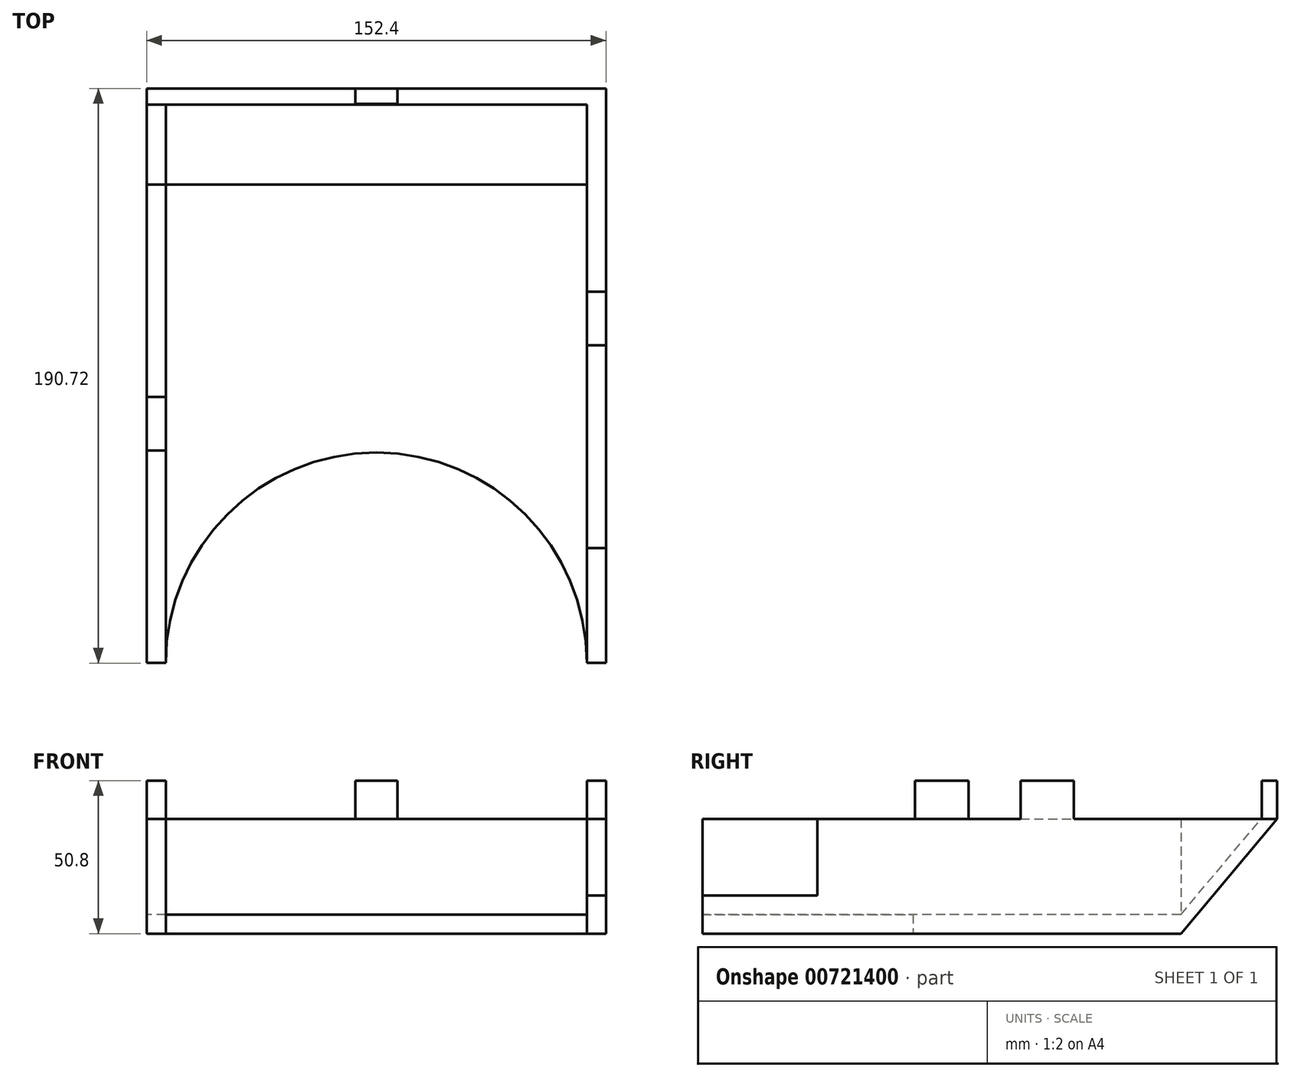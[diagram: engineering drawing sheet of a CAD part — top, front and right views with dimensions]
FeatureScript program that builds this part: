
annotation { "Feature Type Name" : "Feature", "Feature Type Description" : "" }
export const myFeature = defineFeature(function(context is Context, id is Id, definition is map)
    precondition{}
    {
        {
            var Q0;
            Q0=qCreatedBy(makeId("Top.planeOp"),FACE);
            var sketch = newSketch(context, id + "F0", { "sketchPlane" : qUnion([Q0])});
            skLineSegment(sketch, "E0.bottom", {"start": v(76.2, 79.38) * mm, "end": v(-76.2, 79.37) * mm});
            skLineSegment(sketch, "E0.top", {"start": v(76.2, -79.38) * mm, "end": v(-76.2, -79.38) * mm});
            skLineSegment(sketch, "E0.left", {"start": v(76.2, 79.38) * mm, "end": v(76.2, -79.38) * mm});
            skLineSegment(sketch, "E0.right", {"start": v(-76.2, 79.38) * mm, "end": v(-76.2, -79.38) * mm});
            skPoint(sketch, "E0.middle", {"position": v(0, 0) * mm});
            skLineSegment(sketch, "E1", {"start": v(-69.85, -79.38) * mm, "end": v(-69.85, 79.37) * mm});
            skLineSegment(sketch, "E2", {"start": v(69.85, 79.38) * mm, "end": v(69.85, -79.38) * mm});
            skArc(sketch, "E3", {"start": v(69.85, -79.38) * mm, "mid": v(0, -9.52) * mm, "end": v(-69.85, -79.38) * mm});
            skSolve(sketch);
        }
        {
            var Q0;
            {var subQ0=sQuery(id+"F0.wireOp",EDGE,"E1");Q0=makeQuery(id+"F0.imprint","IMPRINT",FACE,{"disambiguationData":[TD([[makeQuery(id+"F0.imprint","IMPRINT",EDGE,{"derivedFrom":subQ0}),-1.0]])]});}
            extrude(context, id + "F1", {"entities" : qUnion([Q0]), "depth" : 6.35 * mm, "offsetDistance" : 25.4 * mm});
        }
        {
            var Q0;
            {var subQ0=sQuery(id+"F0.wireOp",EDGE,"E0.left");Q0=makeQuery(id+"F0.imprint","IMPRINT",FACE,{"disambiguationData":[TD([[makeQuery(id+"F0.imprint","IMPRINT",EDGE,{"derivedFrom":subQ0}),-1.0]])]});}
            var Q1;
            {var subQ0=sQuery(id+"F0.wireOp",EDGE,"E0.right");Q1=makeQuery(id+"F0.imprint","IMPRINT",FACE,{"disambiguationData":[TD([[makeQuery(id+"F0.imprint","IMPRINT",EDGE,{"derivedFrom":subQ0}),1.0]])]});}
            extrude(context, id + "F2", {"entities" : qUnion([Q0, Q1]), "operationType" : NewBodyOperationType.ADD, "depth" : 38.1 * mm, "offsetDistance" : 25.4 * mm});
        }
        {
            var Q0;
            Q0=makeQuery(id+"F2.opExtrude","SWEPT_FACE",FACE,{"disambiguationData":[OSD([sQuery(id+"F0.wireOp",EDGE,"E0.left")])]});
            var sketch = newSketch(context, id + "F3", { "sketchPlane" : qUnion([Q0])});
            skLineSegment(sketch, "E4", {"start": v(79.38, 0) * mm, "end": v(111.34, 38.1) * mm});
            skLineSegment(sketch, "E5", {"start": v(111.34, 38.1) * mm, "end": v(79.38, 38.1) * mm});
            skLineSegment(sketch, "E6", {"start": v(79.38, 6.35) * mm, "end": v(106.02, 38.1) * mm});
            skSolve(sketch);
        }
        {
            var Q0;
            {var subQ0=sQuery(id+"F3.wireOp",EDGE,"E4");Q0=makeQuery(id+"F3.imprint","IMPRINT",FACE,{"disambiguationData":[TD([[makeQuery(id+"F3.imprint","IMPRINT",EDGE,{"derivedFrom":subQ0}),1.0]])]});}
            extrude(context, id + "F4", {"entities" : qUnion([Q0]), "operationType" : NewBodyOperationType.ADD, "oppositeDirection" : true, "depth" : 152.4 * mm, "offsetDistance" : 25.4 * mm});
        }
        {
            var Q0;
            {var subQ4=sQuery(id+"F3.wireOp",EDGE,"E6");Q0=makeQuery(id+"F3.imprint","IMPRINT",FACE,{"disambiguationData":[TD([[makeQuery(id+"F3.imprint","IMPRINT",EDGE,{"derivedFrom":subQ4}),1.0]])]});}
            extrude(context, id + "F5", {"entities" : qUnion([Q0]), "operationType" : NewBodyOperationType.ADD, "oppositeDirection" : true, "depth" : 6.35 * mm, "offsetDistance" : 25.4 * mm});
        }
        {
            var Q0;
            Q0=makeQuery(id+"F4.boolean.opBoolean","MERGE",FACE,{"derivedFrom":[makeQuery(id+"F2.opExtrude","SWEPT_FACE",FACE,{"disambiguationData":[OSD([sQuery(id+"F0.wireOp",EDGE,"E0.right")])]}),makeQuery(id+"F4.opExtrude","CAP_FACE",FACE,{"disambiguationData":[OSD([sQuery(id+"F0.wireOp",EDGE,"E0.bottom"),sQuery(id+"F0.wireOp",EDGE,"E0.left"),sQuery(id+"F3.wireOp",EDGE,"E4"),sQuery(id+"F3.wireOp",EDGE,"E5"),sQuery(id+"F3.wireOp",EDGE,"E6")])],"isStart":false})]});
            var sketch = newSketch(context, id + "F6", { "sketchPlane" : qUnion([Q0])});
            skLineSegment(sketch, "E7", {"start": v(-79.38, 38.1) * mm, "end": v(-106.02, 38.1) * mm});
            skLineSegment(sketch, "E8", {"start": v(-106.02, 38.1) * mm, "end": v(-79.38, 6.35) * mm});
            skLineSegment(sketch, "E9", {"start": v(-79.38, 6.35) * mm, "end": v(-79.38, 38.1) * mm});
            skSolve(sketch);
        }
        {
            var Q0;
            Q0=makeQuery(id+"F6.imprint","IMPRINT",FACE,{"disambiguationData":[TD([[makeQuery(id+"F6.imprint","IMPRINT",EDGE,{"derivedFrom":sQuery(id+"F6.wireOp",EDGE,"E7")}),1.0]])]});
            extrude(context, id + "F7", {"entities" : qUnion([Q0]), "oppositeDirection" : true, "depth" : 6.35 * mm, "offsetDistance" : 25.4 * mm});
        }
        {
            var Q0;
            {var subQ0=sQuery(id+"F0.wireOp",EDGE,"E0.top");Q0=makeQuery(id+"F2.opExtrude","SWEPT_FACE",FACE,{"disambiguationData":[OSD([subQ0]),TDD([makeQuery(id+"F0.imprint","IMPRINT",EDGE,{"disambiguationData":[TD([[makeQuery(id+"F0.imprint","INTERSECT",VERTEX,{"derivedFrom":[subQ0,sQuery(id+"F0.wireOp",EDGE,"E0.left")]}),-1.0]])],"derivedFrom":subQ0})])]});}
            var sketch = newSketch(context, id + "F8", { "sketchPlane" : qUnion([Q0])});
            skLineSegment(sketch, "E10.bottom", {"start": v(69.85, 38.1) * mm, "end": v(76.2, 38.1) * mm});
            skLineSegment(sketch, "E10.top", {"start": v(69.85, 12.7) * mm, "end": v(76.2, 12.7) * mm});
            skLineSegment(sketch, "E10.left", {"start": v(69.85, 38.1) * mm, "end": v(69.85, 12.7) * mm});
            skLineSegment(sketch, "E10.right", {"start": v(76.2, 38.1) * mm, "end": v(76.2, 12.7) * mm});
            skSolve(sketch);
        }
        {
            var Q0;
            Q0=makeQuery(id+"F8.imprint","IMPRINT",FACE,{"disambiguationData":[TD([[makeQuery(id+"F8.imprint","IMPRINT",EDGE,{"derivedFrom":sQuery(id+"F8.wireOp",EDGE,"E10.bottom")}),1.0]])]});
            extrude(context, id + "F9", {"entities" : qUnion([Q0]), "operationType" : NewBodyOperationType.REMOVE, "oppositeDirection" : true, "depth" : 38.1 * mm, "offsetDistance" : 25.4 * mm});
        }
        {
            var Q0;
            {var subQ0=sQuery(id+"F3.wireOp",EDGE,"E5");Q0=makeQuery(id+"F5.boolean.opBoolean","MERGE",FACE,{"derivedFrom":[makeQuery(id+"F2.opExtrude","CAP_FACE",FACE,{"disambiguationData":[OSD([sQuery(id+"F0.wireOp",EDGE,"E0.bottom"),sQuery(id+"F0.wireOp",EDGE,"E0.top"),sQuery(id+"F0.wireOp",EDGE,"E0.left"),sQuery(id+"F0.wireOp",EDGE,"E2")])],"isStart":false}),makeQuery(id+"F4.opExtrude","SWEPT_FACE",FACE,{"disambiguationData":[OSD([subQ0])]}),makeQuery(id+"F5.opExtrude","SWEPT_FACE",FACE,{"disambiguationData":[OSD([subQ0])]})]});}
            var sketch = newSketch(context, id + "F10", { "sketchPlane" : qUnion([Q0])});
            skLineSegment(sketch, "E11.bottom", {"start": v(6.99, 111.34) * mm, "end": v(-6.99, 111.34) * mm});
            skLineSegment(sketch, "E11.top", {"start": v(6.99, 106.26) * mm, "end": v(-6.99, 106.26) * mm});
            skLineSegment(sketch, "E11.left", {"start": v(6.98, 111.34) * mm, "end": v(6.99, 106.26) * mm});
            skLineSegment(sketch, "E11.right", {"start": v(-6.99, 111.34) * mm, "end": v(-6.99, 106.26) * mm});
            skPoint(sketch, "E11.middle", {"position": v(0, 108.8) * mm});
            skPoint(sketch, "E11.middle.positionSnap0", {"position": v(0, 111.34) * mm});
            skPoint(sketch, "E11.centerSnap0", {"position": v(0, 111.34) * mm});
            skLineSegment(sketch, "E12.bottom", {"start": v(76.2, 26.14) * mm, "end": v(69.85, 26.14) * mm});
            skLineSegment(sketch, "E12.top", {"start": v(76.2, 43.92) * mm, "end": v(69.85, 43.92) * mm});
            skLineSegment(sketch, "E12.left", {"start": v(76.2, 26.14) * mm, "end": v(76.2, 43.92) * mm});
            skLineSegment(sketch, "E12.right", {"start": v(69.85, 26.14) * mm, "end": v(69.85, 43.92) * mm});
            skPoint(sketch, "E12.middle", {"position": v(73.03, 35.03) * mm});
            skPoint(sketch, "E12.middle.positionSnap0", {"position": v(76.2, 35.03) * mm});
            skPoint(sketch, "E12.middle.positionSnap1", {"position": v(73.03, -41.27) * mm});
            skPoint(sketch, "E12.centerSnap0", {"position": v(76.2, 35.03) * mm});
            skPoint(sketch, "E12.centerSnap1", {"position": v(73.03, -41.27) * mm});
            skSolve(sketch);
        }
        {
            var Q0;
            Q0=makeQuery(id+"F2.opExtrude","CAP_FACE",FACE,{"disambiguationData":[OSD([sQuery(id+"F0.wireOp",EDGE,"E0.bottom"),sQuery(id+"F0.wireOp",EDGE,"E0.top"),sQuery(id+"F0.wireOp",EDGE,"E0.right"),sQuery(id+"F0.wireOp",EDGE,"E1")])],"isStart":false});
            var sketch = newSketch(context, id + "F11", { "sketchPlane" : qUnion([Q0])});
            skLineSegment(sketch, "E13.bottom", {"start": v(-69.85, -8.89) * mm, "end": v(-76.2, -8.89) * mm});
            skLineSegment(sketch, "E13.top", {"start": v(-69.85, 8.9) * mm, "end": v(-76.2, 8.9) * mm});
            skLineSegment(sketch, "E13.left", {"start": v(-69.85, -8.89) * mm, "end": v(-69.85, 8.9) * mm});
            skLineSegment(sketch, "E13.right", {"start": v(-76.2, -8.89) * mm, "end": v(-76.2, 8.9) * mm});
            skPoint(sketch, "E13.middle", {"position": v(-73.03, 0) * mm});
            skPoint(sketch, "E13.middle.positionSnap0", {"position": v(-69.85, 0) * mm});
            skPoint(sketch, "E13.middle.positionSnap1", {"position": v(-73.03, -79.38) * mm});
            skPoint(sketch, "E13.centerSnap0", {"position": v(-69.85, 0) * mm});
            skPoint(sketch, "E13.centerSnap1", {"position": v(-73.03, -79.38) * mm});
            skSolve(sketch);
        }
        {
            var Q0;
            Q0=makeQuery(id+"F11.imprint","IMPRINT",FACE,{"disambiguationData":[TD([[makeQuery(id+"F11.imprint","IMPRINT",EDGE,{"derivedFrom":sQuery(id+"F11.wireOp",EDGE,"E13.bottom")}),-1.0]])]});
            var Q1;
            Q1=makeQuery(id+"F10.imprint","IMPRINT",FACE,{"disambiguationData":[TD([[makeQuery(id+"F10.imprint","IMPRINT",EDGE,{"derivedFrom":sQuery(id+"F10.wireOp",EDGE,"E12.bottom")}),-1.0]])]});
            var Q2;
            Q2=makeQuery(id+"F10.imprint","IMPRINT",FACE,{"disambiguationData":[TD([[makeQuery(id+"F10.imprint","IMPRINT",EDGE,{"derivedFrom":sQuery(id+"F10.wireOp",EDGE,"E11.bottom")}),-1.0]])]});
            extrude(context, id + "F12", {"entities" : qUnion([Q0, Q1, Q2]), "operationType" : NewBodyOperationType.ADD, "depth" : 12.7 * mm, "offsetDistance" : 25.4 * mm});
        }
    });
